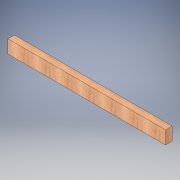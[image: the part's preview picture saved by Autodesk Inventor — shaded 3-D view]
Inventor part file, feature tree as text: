
AUTODESK INVENTOR PART (.ipt)
format: ipt  version: 2017 (Build 210142000, 142)  size: 101,376 bytes
history: native  units: in
note: dims shown in document units (in); Inventor stores cm internally (conversion verified against a paired STEP export)
features: extrude x1, sketch x1
ambient origin geometry x8: Origin, YZ Plane, XZ Plane, XY Plane, X Axis, Y Axis, Z Axis, Center Point
bodies: Solid1 (feature_tree)
feature tree (2):
  extrude  "Extrusion1"  Depth=3.0in
  sketch  "Sketch1"  dims[d0=72.0in d1=3.0in d2=6.0in d3=0.0in]
